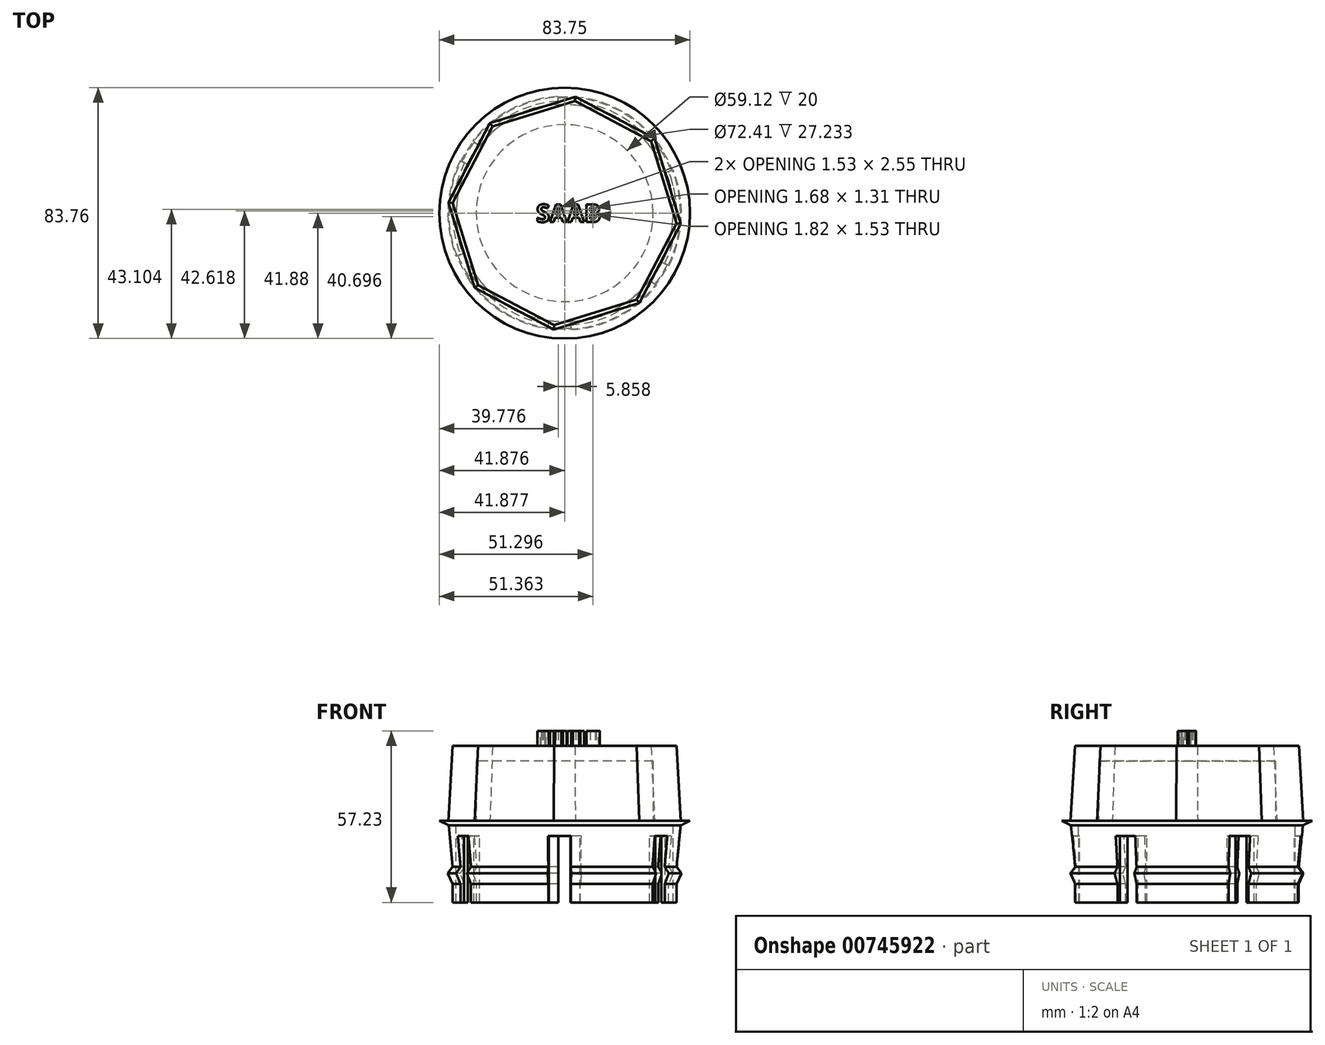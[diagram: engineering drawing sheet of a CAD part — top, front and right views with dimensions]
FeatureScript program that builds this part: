
annotation { "Feature Type Name" : "Feature", "Feature Type Description" : "" }
export const myFeature = defineFeature(function(context is Context, id is Id, definition is map)
    precondition{}
    {
        {
            var Q0;
            Q0=qCreatedBy(makeId("Top.planeOp"),FACE);
            var sketch = newSketch(context, id + "F0", { "sketchPlane" : qUnion([Q0])});
            skCircle(sketch, "E0.cCircle", {"center": v(41.88, 0) * mm, "radius": 39.01 * mm, "construction": true});
            skLineSegment(sketch, "E0.0", {"start": v(11.87, -24.94) * mm, "end": v(3.03, 3.58) * mm});
            skLineSegment(sketch, "E0.1", {"start": v(3.03, 3.58) * mm, "end": v(16.94, 30) * mm});
            skLineSegment(sketch, "E0.2", {"start": v(16.94, 30) * mm, "end": v(45.46, 38.85) * mm});
            skLineSegment(sketch, "E0.3", {"start": v(45.46, 38.85) * mm, "end": v(71.88, 24.94) * mm});
            skLineSegment(sketch, "E0.4", {"start": v(71.88, 24.94) * mm, "end": v(80.72, -3.58) * mm});
            skLineSegment(sketch, "E0.5", {"start": v(80.72, -3.58) * mm, "end": v(66.81, -30) * mm});
            skLineSegment(sketch, "E0.6", {"start": v(66.81, -30) * mm, "end": v(38.3, -38.85) * mm});
            skLineSegment(sketch, "E0.7", {"start": v(38.3, -38.85) * mm, "end": v(11.87, -24.94) * mm});
            skSolve(sketch);
        }
        {
            var Q0;
            Q0=qSketchRegion(id+"F0",true);
            extrude(context, id + "F1", {"entities" : qUnion([Q0]), "depth" : 25 * mm, "offsetDistance" : 25 * mm, "hasDraft" : true, "draftAngle" : 3 * degree, "draftPullDirection" : true});
        }
        {
            var Q0;
            Q0=qCreatedBy(makeId("Front.planeOp"),FACE);
            var sketch = newSketch(context, id + "F2", { "sketchPlane" : qUnion([Q0])});
            skLineSegment(sketch, "E1", {"start": v(75.4, 25) * mm, "end": v(75.4, 26.11) * mm});
            skLineSegment(sketch, "E2", {"start": v(75.4, 26.11) * mm, "end": v(75.15, 26.11) * mm});
            skLineSegment(sketch, "E3", {"start": v(75.15, 26.11) * mm, "end": v(75.15, 25.99) * mm});
            skLineSegment(sketch, "E4", {"start": v(57.94, 28.76) * mm, "end": v(57.94, 28) * mm});
            skLineSegment(sketch, "E5", {"start": v(57.94, 28) * mm, "end": v(41.94, 28) * mm});
            skArc(sketch, "E6", {"start": v(75.15, 25.99) * mm, "mid": v(66.86, 29.36) * mm, "end": v(57.94, 28.76) * mm});
            skLineSegment(sketch, "E7", {"start": v(41.94, 28) * mm, "end": v(41.94, 25) * mm});
            skSolve(sketch);
        }
        {
            var Q0;
            Q0=qSketchRegion(id+"F2",true);
            var Q1;
            Q1=sQuery(id+"F2.wireOp",EDGE,"E5");
            var Q2;
            Q2=sQuery(id+"F2.wireOp",EDGE,"E4");
            var Q3;
            Q3=sQuery(id+"F2.wireOp",EDGE,"E6");
            var Q4;
            Q4=sQuery(id+"F2.wireOp",EDGE,"E1");
            var Q5;
            Q5=sQuery(id+"F2.wireOp",EDGE,"E3");
            var Q6;
            Q6=sQuery(id+"F2.wireOp",EDGE,"E2");
            var Q7;
            Q7=sQuery(id+"F2.wireOp",EDGE,"E7");
            revolve(context, id + "F3", {"bodyType" : ToolBodyType.SURFACE, "surfaceOperationType" : NewSurfaceOperationType.NEW, "entities" : qUnion([Q0]), "surfaceEntities" : qUnion([Q1, Q2, Q3, Q4, Q5, Q6]), "axis" : qUnion([Q7]), "revolveType" : RevolveType.FULL});
        }
        {
            var Q0;
            Q0=qCreatedBy(makeId("Front.planeOp"),FACE);
            var sketch = newSketch(context, id + "F4", { "sketchPlane" : qUnion([Q0])});
            skLineSegment(sketch, "E8", {"start": v(41.88, -0.28) * mm, "end": v(41.88, -0.28) * mm});
            skLineSegment(sketch, "E9", {"start": v(41.88, -0.28) * mm, "end": v(13.92, 0) * mm});
            skLineSegment(sketch, "E10", {"start": v(13.92, 0) * mm, "end": v(5.67, 0) * mm});
            skLineSegment(sketch, "E11", {"start": v(5.67, 0) * mm, "end": v(5.67, -27.23) * mm});
            skLineSegment(sketch, "E12", {"start": v(5.67, -27.23) * mm, "end": v(4.47, -27.23) * mm});
            skLineSegment(sketch, "E13", {"start": v(4.47, -27.23) * mm, "end": v(4.47, -21.1) * mm});
            skLineSegment(sketch, "E14", {"start": v(4.47, -21.1) * mm, "end": v(2.87, -17.52) * mm});
            skLineSegment(sketch, "E15", {"start": v(2.87, -17.52) * mm, "end": v(4.47, -15.39) * mm});
            skLineSegment(sketch, "E16", {"start": v(4.47, -15.39) * mm, "end": v(3.14, -1.54) * mm});
            skLineSegment(sketch, "E17", {"start": v(3.14, -1.54) * mm, "end": v(0, 0) * mm});
            skLineSegment(sketch, "E18", {"start": v(41.88, 0) * mm, "end": v(0, 0) * mm});
            skLineSegment(sketch, "E19", {"start": v(41.88, -0.28) * mm, "end": v(41.88, -22.81) * mm});
            skSolve(sketch);
        }
        {
            var Q0;
            Q0=qSketchRegion(id+"F4",true);
            var Q1;
            Q1=sQuery(id+"F4.wireOp",EDGE,"E18");
            var Q2;
            Q2=sQuery(id+"F4.wireOp",EDGE,"E17");
            var Q3;
            Q3=sQuery(id+"F4.wireOp",EDGE,"E16");
            var Q4;
            Q4=sQuery(id+"F4.wireOp",EDGE,"E15");
            var Q5;
            Q5=sQuery(id+"F4.wireOp",EDGE,"E14");
            var Q6;
            Q6=sQuery(id+"F4.wireOp",EDGE,"E12");
            var Q7;
            Q7=sQuery(id+"F4.wireOp",EDGE,"E13");
            var Q8;
            Q8=sQuery(id+"F4.wireOp",EDGE,"E11");
            var Q9;
            Q9=sQuery(id+"F4.wireOp",EDGE,"E19");
            revolve(context, id + "F5", {"surfaceOperationType" : NewSurfaceOperationType.NEW, "entities" : qUnion([Q0]), "surfaceEntities" : qUnion([Q1, Q2, Q3, Q4, Q5, Q6, Q7, Q8]), "axis" : qUnion([Q9]), "revolveType" : RevolveType.FULL});
        }
        {
            var Q0;
            Q0=qCreatedBy(makeId("Top.planeOp"),FACE);
            var sketch = newSketch(context, id + "F6", { "sketchPlane" : qUnion([Q0])});
            skLineSegment(sketch, "E20", {"start": v(41.81, 0) * mm, "end": v(-12.03, 27.08) * mm});
            skLineSegment(sketch, "E21", {"start": v(-12.03, 27.08) * mm, "end": v(-4.8, 36.77) * mm});
            skLineSegment(sketch, "E22", {"start": v(-4.8, 36.77) * mm, "end": v(41.81, 0) * mm});
            skLineSegment(sketch, "E23.1.0", {"start": v(41.81, 0) * mm, "end": v(-8.56, -33.09) * mm});
            skLineSegment(sketch, "E23.1.1", {"start": v(-8.56, -33.09) * mm, "end": v(-13.34, -21.99) * mm});
            skLineSegment(sketch, "E23.1.2", {"start": v(-13.34, -21.99) * mm, "end": v(41.81, 0) * mm});
            skLineSegment(sketch, "E23.2.0", {"start": v(41.81, 0) * mm, "end": v(45.28, -60.17) * mm});
            skLineSegment(sketch, "E23.2.1", {"start": v(45.28, -60.17) * mm, "end": v(33.28, -58.76) * mm});
            skLineSegment(sketch, "E23.2.2", {"start": v(33.28, -58.76) * mm, "end": v(41.81, 0) * mm});
            skLineSegment(sketch, "E23.3.0", {"start": v(41.81, 0) * mm, "end": v(95.66, -27.08) * mm});
            skLineSegment(sketch, "E23.3.1", {"start": v(95.66, -27.08) * mm, "end": v(88.43, -36.77) * mm});
            skLineSegment(sketch, "E23.3.2", {"start": v(88.43, -36.77) * mm, "end": v(41.81, 0) * mm});
            skLineSegment(sketch, "E23.4.0", {"start": v(41.81, 0) * mm, "end": v(92.2, 33.09) * mm});
            skLineSegment(sketch, "E23.4.1", {"start": v(92.2, 33.09) * mm, "end": v(96.97, 21.99) * mm});
            skLineSegment(sketch, "E23.4.2", {"start": v(96.97, 21.99) * mm, "end": v(41.81, 0) * mm});
            skLineSegment(sketch, "E23.5.0", {"start": v(41.81, 0) * mm, "end": v(38.35, 60.17) * mm});
            skLineSegment(sketch, "E23.5.1", {"start": v(38.35, 60.17) * mm, "end": v(50.35, 58.76) * mm});
            skLineSegment(sketch, "E23.5.2", {"start": v(50.35, 58.76) * mm, "end": v(41.81, 0) * mm});
            skPoint(sketch, "E23.center", {"position": v(41.81, 0) * mm});
            skSolve(sketch);
        }
        {
            var Q0;
            Q0=qSketchRegion(id+"F6",true);
            extrude(context, id + "F7", {"entities" : qUnion([Q0]), "oppositeDirection" : true, "depth" : 35 * mm, "offsetDistance" : 25 * mm});
        }
        {
            var Q0;
            Q0=makeQuery(id+"F7.opExtrude","SWEPT_BODY",BODY,{"disambiguationData":[OSD([sQuery(id+"F6.wireOp",EDGE,"E23.5.0"),sQuery(id+"F6.wireOp",EDGE,"E23.5.1"),sQuery(id+"F6.wireOp",EDGE,"E23.5.2")])]});
            var Q1;
            Q1=makeQuery(id+"F7.opExtrude","SWEPT_BODY",BODY,{"disambiguationData":[OSD([sQuery(id+"F6.wireOp",EDGE,"E23.4.0"),sQuery(id+"F6.wireOp",EDGE,"E23.4.1"),sQuery(id+"F6.wireOp",EDGE,"E23.4.2")])]});
            var Q2;
            Q2=makeQuery(id+"F7.opExtrude","SWEPT_BODY",BODY,{"disambiguationData":[OSD([sQuery(id+"F6.wireOp",EDGE,"E23.3.0"),sQuery(id+"F6.wireOp",EDGE,"E23.3.1"),sQuery(id+"F6.wireOp",EDGE,"E23.3.2")])]});
            var Q3;
            Q3=makeQuery(id+"F7.opExtrude","SWEPT_BODY",BODY,{"disambiguationData":[OSD([sQuery(id+"F6.wireOp",EDGE,"E23.2.0"),sQuery(id+"F6.wireOp",EDGE,"E23.2.1"),sQuery(id+"F6.wireOp",EDGE,"E23.2.2")])]});
            var Q4;
            Q4=makeQuery(id+"F7.opExtrude","SWEPT_BODY",BODY,{"disambiguationData":[OSD([sQuery(id+"F6.wireOp",EDGE,"E23.1.0"),sQuery(id+"F6.wireOp",EDGE,"E23.1.1"),sQuery(id+"F6.wireOp",EDGE,"E23.1.2")])]});
            var Q5;
            Q5=makeQuery(id+"F7.opExtrude","SWEPT_BODY",BODY,{"disambiguationData":[OSD([sQuery(id+"F6.wireOp",EDGE,"E20"),sQuery(id+"F6.wireOp",EDGE,"E21"),sQuery(id+"F6.wireOp",EDGE,"E22")])]});
            var Q6;
            Q6=makeQuery(id+"F5.opRevolve","SWEPT_BODY",BODY,{"disambiguationData":[OSD([sQuery(id+"F4.wireOp",EDGE,"E11"),sQuery(id+"F4.wireOp",EDGE,"E12"),sQuery(id+"F4.wireOp",EDGE,"E13"),sQuery(id+"F4.wireOp",EDGE,"E14"),sQuery(id+"F4.wireOp",EDGE,"E15"),sQuery(id+"F4.wireOp",EDGE,"E16"),sQuery(id+"F4.wireOp",EDGE,"E17"),sQuery(id+"F4.wireOp",EDGE,"E18")])]});
            var Q7;
            Q7=makeQuery(id+"F7.opExtrude","CAP_FACE",FACE,{"disambiguationData":[OSD([sQuery(id+"F6.wireOp",EDGE,"E23.5.0"),sQuery(id+"F6.wireOp",EDGE,"E23.5.1"),sQuery(id+"F6.wireOp",EDGE,"E23.5.2")])],"isStart":true});
            var Q8;
            Q8=makeQuery(id+"F7.opExtrude","CAP_FACE",FACE,{"disambiguationData":[OSD([sQuery(id+"F6.wireOp",EDGE,"E20"),sQuery(id+"F6.wireOp",EDGE,"E21"),sQuery(id+"F6.wireOp",EDGE,"E22")])],"isStart":true});
            var Q9;
            Q9=makeQuery(id+"F7.opExtrude","CAP_FACE",FACE,{"disambiguationData":[OSD([sQuery(id+"F6.wireOp",EDGE,"E23.1.0"),sQuery(id+"F6.wireOp",EDGE,"E23.1.1"),sQuery(id+"F6.wireOp",EDGE,"E23.1.2")])],"isStart":true});
            var Q10;
            Q10=makeQuery(id+"F7.opExtrude","CAP_FACE",FACE,{"disambiguationData":[OSD([sQuery(id+"F6.wireOp",EDGE,"E23.2.0"),sQuery(id+"F6.wireOp",EDGE,"E23.2.1"),sQuery(id+"F6.wireOp",EDGE,"E23.2.2")])],"isStart":true});
            var Q11;
            Q11=makeQuery(id+"F7.opExtrude","CAP_FACE",FACE,{"disambiguationData":[OSD([sQuery(id+"F6.wireOp",EDGE,"E23.3.0"),sQuery(id+"F6.wireOp",EDGE,"E23.3.1"),sQuery(id+"F6.wireOp",EDGE,"E23.3.2")])],"isStart":true});
            var Q12;
            Q12=makeQuery(id+"F7.opExtrude","CAP_FACE",FACE,{"disambiguationData":[OSD([sQuery(id+"F6.wireOp",EDGE,"E23.4.0"),sQuery(id+"F6.wireOp",EDGE,"E23.4.1"),sQuery(id+"F6.wireOp",EDGE,"E23.4.2")])],"isStart":true});
            booleanBodies(context, id + "F8", {"operationType" : BooleanOperationType.SUBTRACTION, "tools" : qUnion([Q0, Q1, Q2, Q3, Q4, Q5]), "targets" : qUnion([Q6]), "offset" : true, "entitiesToOffset" : qUnion([Q7, Q8, Q9, Q10, Q11, Q12]), "offsetDistance" : 5 * mm, "oppositeDirection" : true});
        }
        {
            var Q0;
            Q0=qCreatedBy(makeId("Top.planeOp"),FACE);
            var sketch = newSketch(context, id + "F9", { "sketchPlane" : qUnion([Q0])});
            skCircle(sketch, "E24", {"center": v(41.88, 0) * mm, "radius": 29.56 * mm});
            skSolve(sketch);
        }
        {
            var Q0;
            Q0 = qSketchRegion(id + "F9", true);
            extrude(context, id + "F10", {"entities" : qUnion([Q0]), "operationType" : NewBodyOperationType.REMOVE, "depth" : 20 * mm, "offsetDistance" : 25 * mm});
        }
        {
            var Q0;
            Q0=qCreatedBy(makeId("Top.planeOp"),FACE);
            var sketch = newSketch(context, id + "F11", { "sketchPlane" : qUnion([Q0])});
            skText(sketch, "E25", { "text": "SAAB", "fontName": "OpenSans-Bold.ttf"});
            const initialGuessF11  = {"E25": [0.03239, -0.00298, 1, 0, 0.00593]};
            skSetInitialGuess(sketch, initialGuessF11);
            skSolve(sketch);
        }
        {
            var Q0;
            Q0 = qSketchRegion(id + "F11", true);
            extrude(context, id + "F12", {"entities" : qUnion([Q0]), "depth" : 5 * mm, "offsetDistance" : 25 * mm});
        }
        {
            var Q0;
            Q0=makeQuery(id+"F12.opExtrude","SWEPT_BODY",BODY,{"disambiguationData":[OSD([sQuery(id+"F11.wireOp",EDGE,"E25.sketch_text.stroke-0"),sQuery(id+"F11.wireOp",EDGE,"E25.sketch_text.stroke-1"),sQuery(id+"F11.wireOp",EDGE,"E25.sketch_text.stroke-2"),sQuery(id+"F11.wireOp",EDGE,"E25.sketch_text.stroke-3"),sQuery(id+"F11.wireOp",EDGE,"E25.sketch_text.stroke-4"),sQuery(id+"F11.wireOp",EDGE,"E25.sketch_text.stroke-5"),sQuery(id+"F11.wireOp",EDGE,"E25.sketch_text.stroke-6"),sQuery(id+"F11.wireOp",EDGE,"E25.sketch_text.stroke-7"),sQuery(id+"F11.wireOp",EDGE,"E25.sketch_text.stroke-8"),sQuery(id+"F11.wireOp",EDGE,"E25.sketch_text.stroke-9"),sQuery(id+"F11.wireOp",EDGE,"E25.sketch_text.stroke-10"),sQuery(id+"F11.wireOp",EDGE,"E25.sketch_text.stroke-11"),sQuery(id+"F11.wireOp",EDGE,"E25.sketch_text.stroke-12"),sQuery(id+"F11.wireOp",EDGE,"E25.sketch_text.stroke-13"),sQuery(id+"F11.wireOp",EDGE,"E25.sketch_text.stroke-14"),sQuery(id+"F11.wireOp",EDGE,"E25.sketch_text.stroke-15"),sQuery(id+"F11.wireOp",EDGE,"E25.sketch_text.stroke-16"),sQuery(id+"F11.wireOp",EDGE,"E25.sketch_text.stroke-17"),sQuery(id+"F11.wireOp",EDGE,"E25.sketch_text.stroke-18"),sQuery(id+"F11.wireOp",EDGE,"E25.sketch_text.stroke-19"),sQuery(id+"F11.wireOp",EDGE,"E25.sketch_text.stroke-20"),sQuery(id+"F11.wireOp",EDGE,"E25.sketch_text.stroke-21"),sQuery(id+"F11.wireOp",EDGE,"E25.sketch_text.stroke-22"),sQuery(id+"F11.wireOp",EDGE,"E25.sketch_text.stroke-23"),sQuery(id+"F11.wireOp",EDGE,"E25.sketch_text.stroke-24"),sQuery(id+"F11.wireOp",EDGE,"E25.sketch_text.stroke-25"),sQuery(id+"F11.wireOp",EDGE,"E25.sketch_text.stroke-26"),sQuery(id+"F11.wireOp",EDGE,"E25.sketch_text.stroke-27")])]});
            var Q1;
            Q1=makeQuery(id+"F12.opExtrude","SWEPT_BODY",BODY,{"disambiguationData":[OSD([sQuery(id+"F11.wireOp",EDGE,"E25.sketch_text.stroke-28"),sQuery(id+"F11.wireOp",EDGE,"E25.sketch_text.stroke-29"),sQuery(id+"F11.wireOp",EDGE,"E25.sketch_text.stroke-30"),sQuery(id+"F11.wireOp",EDGE,"E25.sketch_text.stroke-31"),sQuery(id+"F11.wireOp",EDGE,"E25.sketch_text.stroke-32"),sQuery(id+"F11.wireOp",EDGE,"E25.sketch_text.stroke-33"),sQuery(id+"F11.wireOp",EDGE,"E25.sketch_text.stroke-34"),sQuery(id+"F11.wireOp",EDGE,"E25.sketch_text.stroke-35"),sQuery(id+"F11.wireOp",EDGE,"E25.sketch_text.stroke-36"),sQuery(id+"F11.wireOp",EDGE,"E25.sketch_text.stroke-37"),sQuery(id+"F11.wireOp",EDGE,"E25.sketch_text.stroke-38"),sQuery(id+"F11.wireOp",EDGE,"E25.sketch_text.stroke-39")])]});
            var Q2;
            Q2=makeQuery(id+"F12.opExtrude","SWEPT_BODY",BODY,{"disambiguationData":[OSD([sQuery(id+"F11.wireOp",EDGE,"E25.sketch_text.stroke-40"),sQuery(id+"F11.wireOp",EDGE,"E25.sketch_text.stroke-41"),sQuery(id+"F11.wireOp",EDGE,"E25.sketch_text.stroke-42"),sQuery(id+"F11.wireOp",EDGE,"E25.sketch_text.stroke-43"),sQuery(id+"F11.wireOp",EDGE,"E25.sketch_text.stroke-44"),sQuery(id+"F11.wireOp",EDGE,"E25.sketch_text.stroke-45"),sQuery(id+"F11.wireOp",EDGE,"E25.sketch_text.stroke-46"),sQuery(id+"F11.wireOp",EDGE,"E25.sketch_text.stroke-47"),sQuery(id+"F11.wireOp",EDGE,"E25.sketch_text.stroke-48"),sQuery(id+"F11.wireOp",EDGE,"E25.sketch_text.stroke-49"),sQuery(id+"F11.wireOp",EDGE,"E25.sketch_text.stroke-50"),sQuery(id+"F11.wireOp",EDGE,"E25.sketch_text.stroke-51")])]});
            var Q3;
            Q3=makeQuery(id+"F12.opExtrude","SWEPT_BODY",BODY,{"disambiguationData":[OSD([sQuery(id+"F11.wireOp",EDGE,"E25.sketch_text.stroke-52"),sQuery(id+"F11.wireOp",EDGE,"E25.sketch_text.stroke-53"),sQuery(id+"F11.wireOp",EDGE,"E25.sketch_text.stroke-54"),sQuery(id+"F11.wireOp",EDGE,"E25.sketch_text.stroke-55"),sQuery(id+"F11.wireOp",EDGE,"E25.sketch_text.stroke-56"),sQuery(id+"F11.wireOp",EDGE,"E25.sketch_text.stroke-57"),sQuery(id+"F11.wireOp",EDGE,"E25.sketch_text.stroke-58"),sQuery(id+"F11.wireOp",EDGE,"E25.sketch_text.stroke-59"),sQuery(id+"F11.wireOp",EDGE,"E25.sketch_text.stroke-60"),sQuery(id+"F11.wireOp",EDGE,"E25.sketch_text.stroke-61"),sQuery(id+"F11.wireOp",EDGE,"E25.sketch_text.stroke-62"),sQuery(id+"F11.wireOp",EDGE,"E25.sketch_text.stroke-63"),sQuery(id+"F11.wireOp",EDGE,"E25.sketch_text.stroke-64"),sQuery(id+"F11.wireOp",EDGE,"E25.sketch_text.stroke-65"),sQuery(id+"F11.wireOp",EDGE,"E25.sketch_text.stroke-66"),sQuery(id+"F11.wireOp",EDGE,"E25.sketch_text.stroke-67"),sQuery(id+"F11.wireOp",EDGE,"E25.sketch_text.stroke-68"),sQuery(id+"F11.wireOp",EDGE,"E25.sketch_text.stroke-69"),sQuery(id+"F11.wireOp",EDGE,"E25.sketch_text.stroke-70"),sQuery(id+"F11.wireOp",EDGE,"E25.sketch_text.stroke-71"),sQuery(id+"F11.wireOp",EDGE,"E25.sketch_text.stroke-72"),sQuery(id+"F11.wireOp",EDGE,"E25.sketch_text.stroke-73"),sQuery(id+"F11.wireOp",EDGE,"E25.sketch_text.stroke-74"),sQuery(id+"F11.wireOp",EDGE,"E25.sketch_text.stroke-75"),sQuery(id+"F11.wireOp",EDGE,"E25.sketch_text.stroke-76")])]});
            transform(context, id + "F13", {"entities" : qUnion([Q0, Q1, Q2, Q3]), "transformType" : TransformType.TRANSLATION_3D, "dx" : 0 * mm, "dy" : 0 * mm, "dz" : 25 * mm, "makeCopy" : false});
        }
    });
